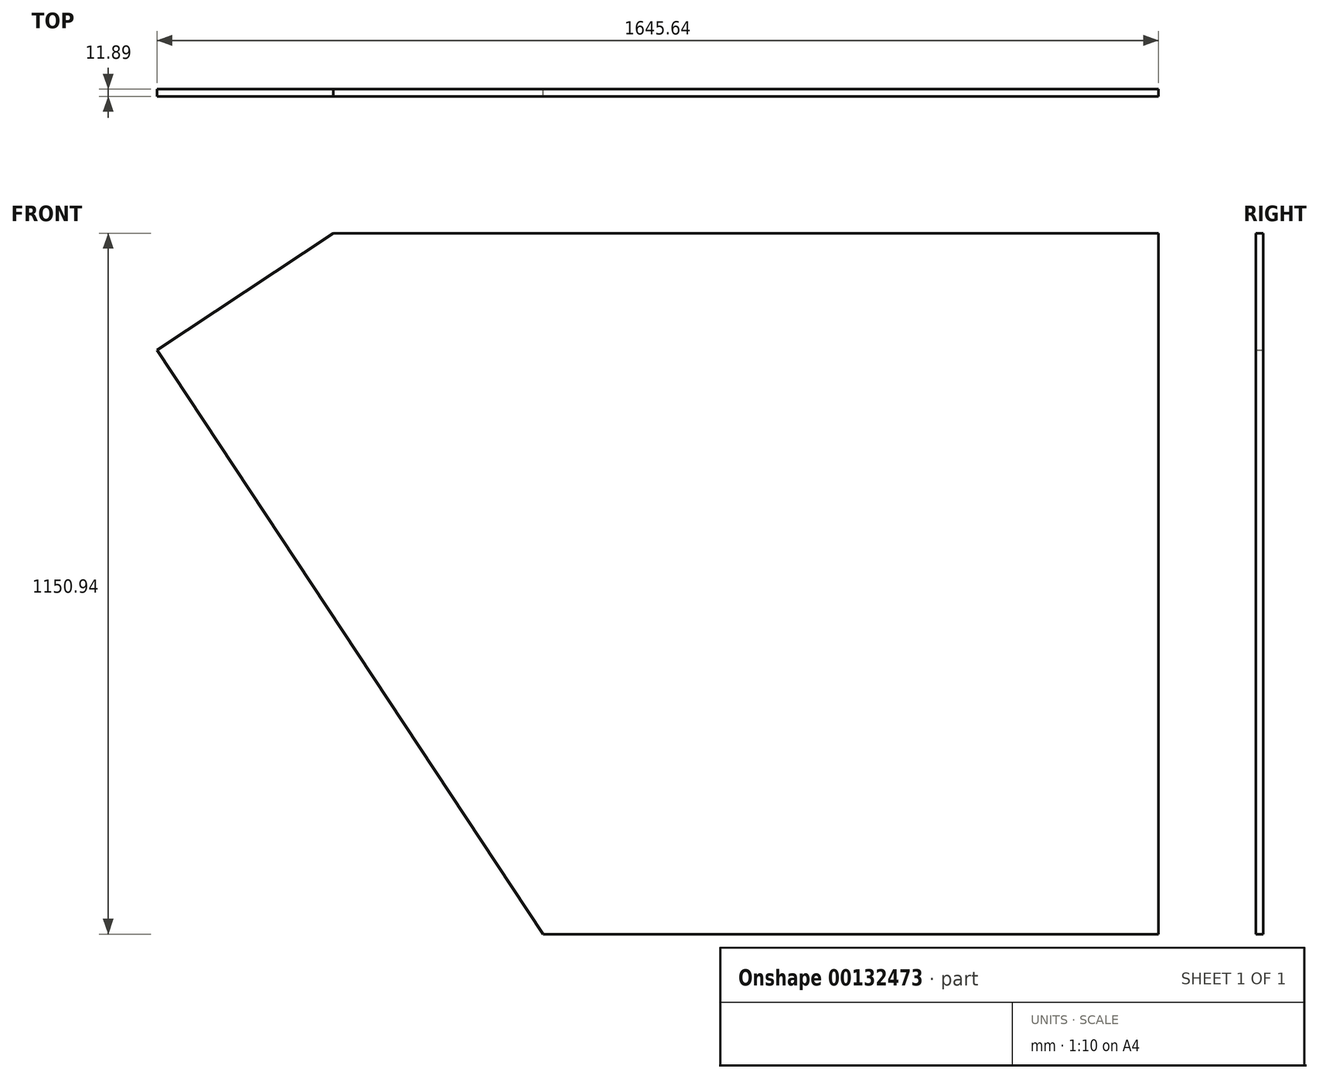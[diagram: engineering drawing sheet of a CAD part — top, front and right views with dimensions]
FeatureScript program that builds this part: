
annotation { "Feature Type Name" : "Feature", "Feature Type Description" : "" }
export const myFeature = defineFeature(function(context is Context, id is Id, definition is map)
    precondition{}
    {
        {
            var Q0;
            Q0=qCreatedBy(makeId("Front.planeOp"),FACE);
            var sketch = newSketch(context, id + "F0", { "sketchPlane" : qUnion([Q0])});
            skLineSegment(sketch, "E0", {"start": v(0, 0) * mm, "end": v(-1010.85, 0) * mm});
            skLineSegment(sketch, "E1", {"start": v(-1010.85, 0) * mm, "end": v(-1645.64, 959.05) * mm});
            skLineSegment(sketch, "E2", {"start": v(-1645.64, 959.05) * mm, "end": v(-1355.73, 1150.94) * mm});
            skLineSegment(sketch, "E3", {"start": v(-1355.73, 1150.94) * mm, "end": v(0, 1150.94) * mm});
            skLineSegment(sketch, "E4", {"start": v(0, 1150.94) * mm, "end": v(0, 0) * mm});
            skSolve(sketch);
        }
        {
            var Q0;
            Q0 = qSketchRegion(id + "F0", true);
            extrude(context, id + "F1", {"entities" : qUnion([Q0]), "depth" : 11.9 * mm});
        }
    });
